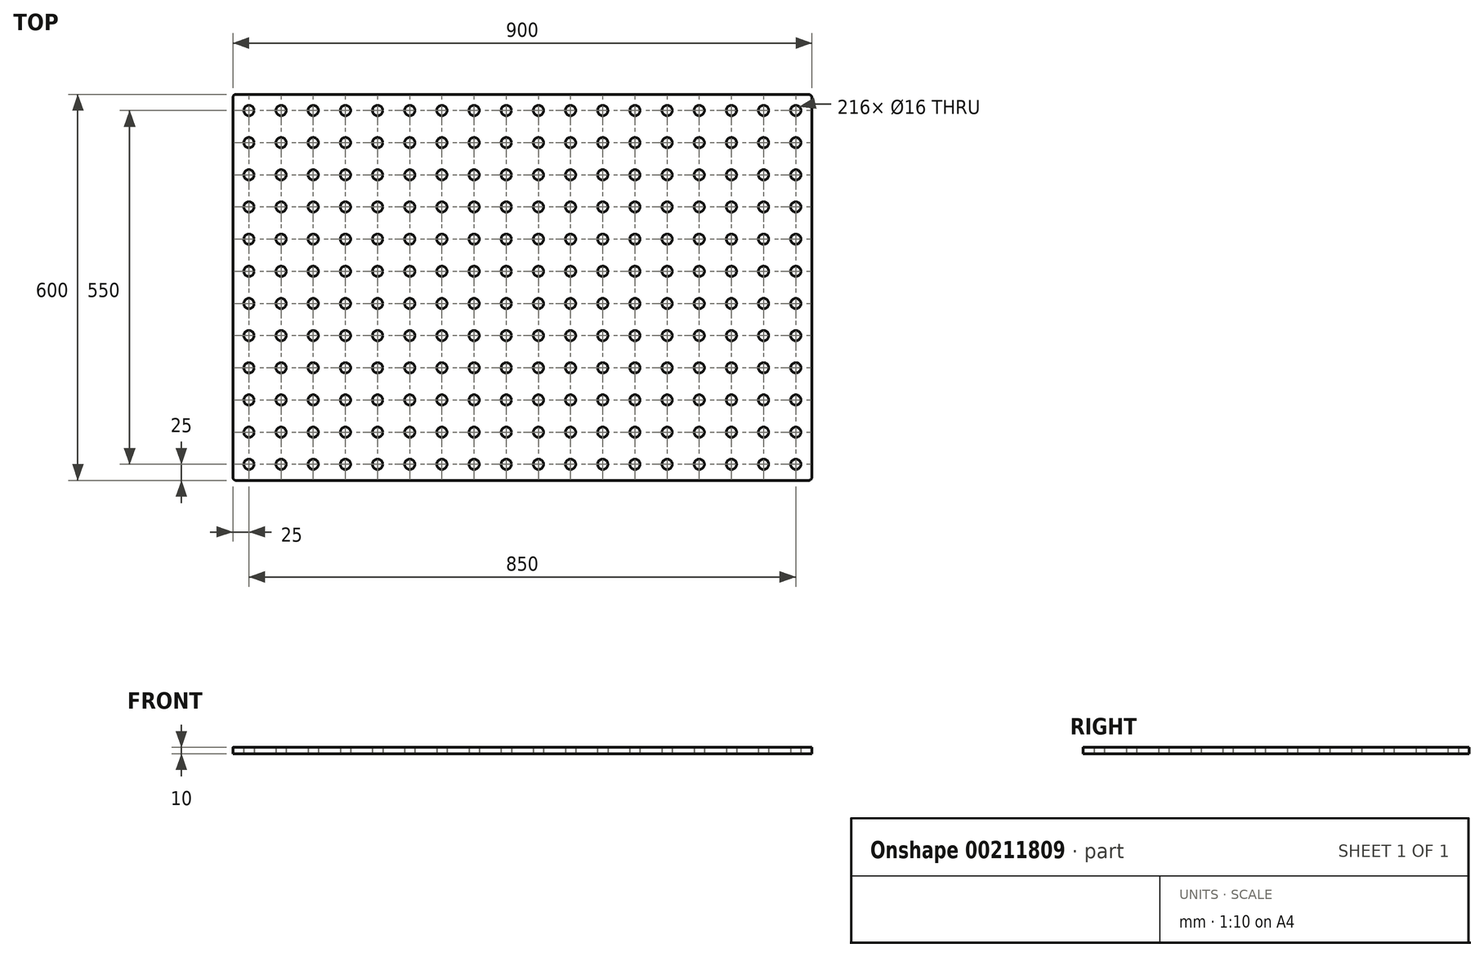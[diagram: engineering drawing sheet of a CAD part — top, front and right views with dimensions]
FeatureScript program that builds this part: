
annotation { "Feature Type Name" : "Feature", "Feature Type Description" : "" }
export const myFeature = defineFeature(function(context is Context, id is Id, definition is map)
    precondition{}
    {
        {
            var Q0;
            Q0=qCreatedBy(makeId("Top.planeOp"),FACE);
            var sketch = newSketch(context, id + "F0", { "sketchPlane" : qUnion([Q0])});
            skLineSegment(sketch, "E0.bottom", {"start": v(5, 0) * mm, "end": v(895, 0) * mm});
            skLineSegment(sketch, "E0.top", {"start": v(5, 600) * mm, "end": v(895, 600) * mm});
            skLineSegment(sketch, "E0.left", {"start": v(0, 5) * mm, "end": v(0, 595) * mm});
            skLineSegment(sketch, "E0.right", {"start": v(900, 5) * mm, "end": v(900, 595) * mm});
            skCircle(sketch, "E1", {"center": v(25, 575) * mm, "radius": 8 * mm});
            skCircle(sketch, "E2.0.1.0", {"center": v(25, 525) * mm, "radius": 8 * mm});
            skCircle(sketch, "E2.0.2.0", {"center": v(25, 475) * mm, "radius": 8 * mm});
            skCircle(sketch, "E2.0.3.0", {"center": v(25, 425) * mm, "radius": 8 * mm});
            skCircle(sketch, "E2.0.4.0", {"center": v(25, 375) * mm, "radius": 8 * mm});
            skCircle(sketch, "E2.0.5.0", {"center": v(25, 325) * mm, "radius": 8 * mm});
            skCircle(sketch, "E2.0.6.0", {"center": v(25, 275) * mm, "radius": 8 * mm});
            skCircle(sketch, "E2.0.7.0", {"center": v(25, 225) * mm, "radius": 8 * mm});
            skCircle(sketch, "E2.0.8.0", {"center": v(25, 175) * mm, "radius": 8 * mm});
            skCircle(sketch, "E2.0.9.0", {"center": v(25, 125) * mm, "radius": 8 * mm});
            skCircle(sketch, "E2.0.10.0", {"center": v(25, 75) * mm, "radius": 8 * mm});
            skCircle(sketch, "E2.0.11.0", {"center": v(25, 25) * mm, "radius": 8 * mm});
            skCircle(sketch, "E2.1.0.0", {"center": v(75, 575) * mm, "radius": 8 * mm});
            skCircle(sketch, "E2.1.1.0", {"center": v(75, 525) * mm, "radius": 8 * mm});
            skCircle(sketch, "E2.1.2.0", {"center": v(75, 475) * mm, "radius": 8 * mm});
            skCircle(sketch, "E2.1.3.0", {"center": v(75, 425) * mm, "radius": 8 * mm});
            skCircle(sketch, "E2.1.4.0", {"center": v(75, 375) * mm, "radius": 8 * mm});
            skCircle(sketch, "E2.1.5.0", {"center": v(75, 325) * mm, "radius": 8 * mm});
            skCircle(sketch, "E2.1.6.0", {"center": v(75, 275) * mm, "radius": 8 * mm});
            skCircle(sketch, "E2.1.7.0", {"center": v(75, 225) * mm, "radius": 8 * mm});
            skCircle(sketch, "E2.1.8.0", {"center": v(75, 175) * mm, "radius": 8 * mm});
            skCircle(sketch, "E2.1.9.0", {"center": v(75, 125) * mm, "radius": 8 * mm});
            skCircle(sketch, "E2.1.10.0", {"center": v(75, 75) * mm, "radius": 8 * mm});
            skCircle(sketch, "E2.1.11.0", {"center": v(75, 25) * mm, "radius": 8 * mm});
            skCircle(sketch, "E2.2.0.0", {"center": v(125, 575) * mm, "radius": 8 * mm});
            skCircle(sketch, "E2.2.1.0", {"center": v(125, 525) * mm, "radius": 8 * mm});
            skCircle(sketch, "E2.2.2.0", {"center": v(125, 475) * mm, "radius": 8 * mm});
            skCircle(sketch, "E2.2.3.0", {"center": v(125, 425) * mm, "radius": 8 * mm});
            skCircle(sketch, "E2.2.4.0", {"center": v(125, 375) * mm, "radius": 8 * mm});
            skCircle(sketch, "E2.2.5.0", {"center": v(125, 325) * mm, "radius": 8 * mm});
            skCircle(sketch, "E2.2.6.0", {"center": v(125, 275) * mm, "radius": 8 * mm});
            skCircle(sketch, "E2.2.7.0", {"center": v(125, 225) * mm, "radius": 8 * mm});
            skCircle(sketch, "E2.2.8.0", {"center": v(125, 175) * mm, "radius": 8 * mm});
            skCircle(sketch, "E2.2.9.0", {"center": v(125, 125) * mm, "radius": 8 * mm});
            skCircle(sketch, "E2.2.10.0", {"center": v(125, 75) * mm, "radius": 8 * mm});
            skCircle(sketch, "E2.2.11.0", {"center": v(125, 25) * mm, "radius": 8 * mm});
            skCircle(sketch, "E2.3.0.0", {"center": v(175, 575) * mm, "radius": 8 * mm});
            skCircle(sketch, "E2.3.1.0", {"center": v(175, 525) * mm, "radius": 8 * mm});
            skCircle(sketch, "E2.3.2.0", {"center": v(175, 475) * mm, "radius": 8 * mm});
            skCircle(sketch, "E2.3.3.0", {"center": v(175, 425) * mm, "radius": 8 * mm});
            skCircle(sketch, "E2.3.4.0", {"center": v(175, 375) * mm, "radius": 8 * mm});
            skCircle(sketch, "E2.3.5.0", {"center": v(175, 325) * mm, "radius": 8 * mm});
            skCircle(sketch, "E2.3.6.0", {"center": v(175, 275) * mm, "radius": 8 * mm});
            skCircle(sketch, "E2.3.7.0", {"center": v(175, 225) * mm, "radius": 8 * mm});
            skCircle(sketch, "E2.3.8.0", {"center": v(175, 175) * mm, "radius": 8 * mm});
            skCircle(sketch, "E2.3.9.0", {"center": v(175, 125) * mm, "radius": 8 * mm});
            skCircle(sketch, "E2.3.10.0", {"center": v(175, 75) * mm, "radius": 8 * mm});
            skCircle(sketch, "E2.3.11.0", {"center": v(175, 25) * mm, "radius": 8 * mm});
            skCircle(sketch, "E2.4.0.0", {"center": v(225, 575) * mm, "radius": 8 * mm});
            skCircle(sketch, "E2.4.1.0", {"center": v(225, 525) * mm, "radius": 8 * mm});
            skCircle(sketch, "E2.4.2.0", {"center": v(225, 475) * mm, "radius": 8 * mm});
            skCircle(sketch, "E2.4.3.0", {"center": v(225, 425) * mm, "radius": 8 * mm});
            skCircle(sketch, "E2.4.4.0", {"center": v(225, 375) * mm, "radius": 8 * mm});
            skCircle(sketch, "E2.4.5.0", {"center": v(225, 325) * mm, "radius": 8 * mm});
            skCircle(sketch, "E2.4.6.0", {"center": v(225, 275) * mm, "radius": 8 * mm});
            skCircle(sketch, "E2.4.7.0", {"center": v(225, 225) * mm, "radius": 8 * mm});
            skCircle(sketch, "E2.4.8.0", {"center": v(225, 175) * mm, "radius": 8 * mm});
            skCircle(sketch, "E2.4.9.0", {"center": v(225, 125) * mm, "radius": 8 * mm});
            skCircle(sketch, "E2.4.10.0", {"center": v(225, 75) * mm, "radius": 8 * mm});
            skCircle(sketch, "E2.4.11.0", {"center": v(225, 25) * mm, "radius": 8 * mm});
            skCircle(sketch, "E2.5.0.0", {"center": v(275, 575) * mm, "radius": 8 * mm});
            skCircle(sketch, "E2.5.1.0", {"center": v(275, 525) * mm, "radius": 8 * mm});
            skCircle(sketch, "E2.5.2.0", {"center": v(275, 475) * mm, "radius": 8 * mm});
            skCircle(sketch, "E2.5.3.0", {"center": v(275, 425) * mm, "radius": 8 * mm});
            skCircle(sketch, "E2.5.4.0", {"center": v(275, 375) * mm, "radius": 8 * mm});
            skCircle(sketch, "E2.5.5.0", {"center": v(275, 325) * mm, "radius": 8 * mm});
            skCircle(sketch, "E2.5.6.0", {"center": v(275, 275) * mm, "radius": 8 * mm});
            skCircle(sketch, "E2.5.7.0", {"center": v(275, 225) * mm, "radius": 8 * mm});
            skCircle(sketch, "E2.5.8.0", {"center": v(275, 175) * mm, "radius": 8 * mm});
            skCircle(sketch, "E2.5.9.0", {"center": v(275, 125) * mm, "radius": 8 * mm});
            skCircle(sketch, "E2.5.10.0", {"center": v(275, 75) * mm, "radius": 8 * mm});
            skCircle(sketch, "E2.5.11.0", {"center": v(275, 25) * mm, "radius": 8 * mm});
            skCircle(sketch, "E2.6.0.0", {"center": v(325, 575) * mm, "radius": 8 * mm});
            skCircle(sketch, "E2.6.1.0", {"center": v(325, 525) * mm, "radius": 8 * mm});
            skCircle(sketch, "E2.6.2.0", {"center": v(325, 475) * mm, "radius": 8 * mm});
            skCircle(sketch, "E2.6.3.0", {"center": v(325, 425) * mm, "radius": 8 * mm});
            skCircle(sketch, "E2.6.4.0", {"center": v(325, 375) * mm, "radius": 8 * mm});
            skCircle(sketch, "E2.6.5.0", {"center": v(325, 325) * mm, "radius": 8 * mm});
            skCircle(sketch, "E2.6.6.0", {"center": v(325, 275) * mm, "radius": 8 * mm});
            skCircle(sketch, "E2.6.7.0", {"center": v(325, 225) * mm, "radius": 8 * mm});
            skCircle(sketch, "E2.6.8.0", {"center": v(325, 175) * mm, "radius": 8 * mm});
            skCircle(sketch, "E2.6.9.0", {"center": v(325, 125) * mm, "radius": 8 * mm});
            skCircle(sketch, "E2.6.10.0", {"center": v(325, 75) * mm, "radius": 8 * mm});
            skCircle(sketch, "E2.6.11.0", {"center": v(325, 25) * mm, "radius": 8 * mm});
            skCircle(sketch, "E2.7.0.0", {"center": v(375, 575) * mm, "radius": 8 * mm});
            skCircle(sketch, "E2.7.1.0", {"center": v(375, 525) * mm, "radius": 8 * mm});
            skCircle(sketch, "E2.7.2.0", {"center": v(375, 475) * mm, "radius": 8 * mm});
            skCircle(sketch, "E2.7.3.0", {"center": v(375, 425) * mm, "radius": 8 * mm});
            skCircle(sketch, "E2.7.4.0", {"center": v(375, 375) * mm, "radius": 8 * mm});
            skCircle(sketch, "E2.7.5.0", {"center": v(375, 325) * mm, "radius": 8 * mm});
            skCircle(sketch, "E2.7.6.0", {"center": v(375, 275) * mm, "radius": 8 * mm});
            skCircle(sketch, "E2.7.7.0", {"center": v(375, 225) * mm, "radius": 8 * mm});
            skCircle(sketch, "E2.7.8.0", {"center": v(375, 175) * mm, "radius": 8 * mm});
            skCircle(sketch, "E2.7.9.0", {"center": v(375, 125) * mm, "radius": 8 * mm});
            skCircle(sketch, "E2.7.10.0", {"center": v(375, 75) * mm, "radius": 8 * mm});
            skCircle(sketch, "E2.7.11.0", {"center": v(375, 25) * mm, "radius": 8 * mm});
            skCircle(sketch, "E2.8.0.0", {"center": v(425, 575) * mm, "radius": 8 * mm});
            skCircle(sketch, "E2.8.1.0", {"center": v(425, 525) * mm, "radius": 8 * mm});
            skCircle(sketch, "E2.8.2.0", {"center": v(425, 475) * mm, "radius": 8 * mm});
            skCircle(sketch, "E2.8.3.0", {"center": v(425, 425) * mm, "radius": 8 * mm});
            skCircle(sketch, "E2.8.4.0", {"center": v(425, 375) * mm, "radius": 8 * mm});
            skCircle(sketch, "E2.8.5.0", {"center": v(425, 325) * mm, "radius": 8 * mm});
            skCircle(sketch, "E2.8.6.0", {"center": v(425, 275) * mm, "radius": 8 * mm});
            skCircle(sketch, "E2.8.7.0", {"center": v(425, 225) * mm, "radius": 8 * mm});
            skCircle(sketch, "E2.8.8.0", {"center": v(425, 175) * mm, "radius": 8 * mm});
            skCircle(sketch, "E2.8.9.0", {"center": v(425, 125) * mm, "radius": 8 * mm});
            skCircle(sketch, "E2.8.10.0", {"center": v(425, 75) * mm, "radius": 8 * mm});
            skCircle(sketch, "E2.8.11.0", {"center": v(425, 25) * mm, "radius": 8 * mm});
            skCircle(sketch, "E2.9.0.0", {"center": v(475, 575) * mm, "radius": 8 * mm});
            skCircle(sketch, "E2.9.1.0", {"center": v(475, 525) * mm, "radius": 8 * mm});
            skCircle(sketch, "E2.9.2.0", {"center": v(475, 475) * mm, "radius": 8 * mm});
            skCircle(sketch, "E2.9.3.0", {"center": v(475, 425) * mm, "radius": 8 * mm});
            skCircle(sketch, "E2.9.4.0", {"center": v(475, 375) * mm, "radius": 8 * mm});
            skCircle(sketch, "E2.9.5.0", {"center": v(475, 325) * mm, "radius": 8 * mm});
            skCircle(sketch, "E2.9.6.0", {"center": v(475, 275) * mm, "radius": 8 * mm});
            skCircle(sketch, "E2.9.7.0", {"center": v(475, 225) * mm, "radius": 8 * mm});
            skCircle(sketch, "E2.9.8.0", {"center": v(475, 175) * mm, "radius": 8 * mm});
            skCircle(sketch, "E2.9.9.0", {"center": v(475, 125) * mm, "radius": 8 * mm});
            skCircle(sketch, "E2.9.10.0", {"center": v(475, 75) * mm, "radius": 8 * mm});
            skCircle(sketch, "E2.9.11.0", {"center": v(475, 25) * mm, "radius": 8 * mm});
            skCircle(sketch, "E2.10.0.0", {"center": v(525, 575) * mm, "radius": 8 * mm});
            skCircle(sketch, "E2.10.1.0", {"center": v(525, 525) * mm, "radius": 8 * mm});
            skCircle(sketch, "E2.10.2.0", {"center": v(525, 475) * mm, "radius": 8 * mm});
            skCircle(sketch, "E2.10.3.0", {"center": v(525, 425) * mm, "radius": 8 * mm});
            skCircle(sketch, "E2.10.4.0", {"center": v(525, 375) * mm, "radius": 8 * mm});
            skCircle(sketch, "E2.10.5.0", {"center": v(525, 325) * mm, "radius": 8 * mm});
            skCircle(sketch, "E2.10.6.0", {"center": v(525, 275) * mm, "radius": 8 * mm});
            skCircle(sketch, "E2.10.7.0", {"center": v(525, 225) * mm, "radius": 8 * mm});
            skCircle(sketch, "E2.10.8.0", {"center": v(525, 175) * mm, "radius": 8 * mm});
            skCircle(sketch, "E2.10.9.0", {"center": v(525, 125) * mm, "radius": 8 * mm});
            skCircle(sketch, "E2.10.10.0", {"center": v(525, 75) * mm, "radius": 8 * mm});
            skCircle(sketch, "E2.10.11.0", {"center": v(525, 25) * mm, "radius": 8 * mm});
            skCircle(sketch, "E2.11.0.0", {"center": v(575, 575) * mm, "radius": 8 * mm});
            skCircle(sketch, "E2.11.1.0", {"center": v(575, 525) * mm, "radius": 8 * mm});
            skCircle(sketch, "E2.11.2.0", {"center": v(575, 475) * mm, "radius": 8 * mm});
            skCircle(sketch, "E2.11.3.0", {"center": v(575, 425) * mm, "radius": 8 * mm});
            skCircle(sketch, "E2.11.4.0", {"center": v(575, 375) * mm, "radius": 8 * mm});
            skCircle(sketch, "E2.11.5.0", {"center": v(575, 325) * mm, "radius": 8 * mm});
            skCircle(sketch, "E2.11.6.0", {"center": v(575, 275) * mm, "radius": 8 * mm});
            skCircle(sketch, "E2.11.7.0", {"center": v(575, 225) * mm, "radius": 8 * mm});
            skCircle(sketch, "E2.11.8.0", {"center": v(575, 175) * mm, "radius": 8 * mm});
            skCircle(sketch, "E2.11.9.0", {"center": v(575, 125) * mm, "radius": 8 * mm});
            skCircle(sketch, "E2.11.10.0", {"center": v(575, 75) * mm, "radius": 8 * mm});
            skCircle(sketch, "E2.11.11.0", {"center": v(575, 25) * mm, "radius": 8 * mm});
            skCircle(sketch, "E2.12.0.0", {"center": v(625, 575) * mm, "radius": 8 * mm});
            skCircle(sketch, "E2.12.1.0", {"center": v(625, 525) * mm, "radius": 8 * mm});
            skCircle(sketch, "E2.12.2.0", {"center": v(625, 475) * mm, "radius": 8 * mm});
            skCircle(sketch, "E2.12.3.0", {"center": v(625, 425) * mm, "radius": 8 * mm});
            skCircle(sketch, "E2.12.4.0", {"center": v(625, 375) * mm, "radius": 8 * mm});
            skCircle(sketch, "E2.12.5.0", {"center": v(625, 325) * mm, "radius": 8 * mm});
            skCircle(sketch, "E2.12.6.0", {"center": v(625, 275) * mm, "radius": 8 * mm});
            skCircle(sketch, "E2.12.7.0", {"center": v(625, 225) * mm, "radius": 8 * mm});
            skCircle(sketch, "E2.12.8.0", {"center": v(625, 175) * mm, "radius": 8 * mm});
            skCircle(sketch, "E2.12.9.0", {"center": v(625, 125) * mm, "radius": 8 * mm});
            skCircle(sketch, "E2.12.10.0", {"center": v(625, 75) * mm, "radius": 8 * mm});
            skCircle(sketch, "E2.12.11.0", {"center": v(625, 25) * mm, "radius": 8 * mm});
            skCircle(sketch, "E2.13.0.0", {"center": v(675, 575) * mm, "radius": 8 * mm});
            skCircle(sketch, "E2.13.1.0", {"center": v(675, 525) * mm, "radius": 8 * mm});
            skCircle(sketch, "E2.13.2.0", {"center": v(675, 475) * mm, "radius": 8 * mm});
            skCircle(sketch, "E2.13.3.0", {"center": v(675, 425) * mm, "radius": 8 * mm});
            skCircle(sketch, "E2.13.4.0", {"center": v(675, 375) * mm, "radius": 8 * mm});
            skCircle(sketch, "E2.13.5.0", {"center": v(675, 325) * mm, "radius": 8 * mm});
            skCircle(sketch, "E2.13.6.0", {"center": v(675, 275) * mm, "radius": 8 * mm});
            skCircle(sketch, "E2.13.7.0", {"center": v(675, 225) * mm, "radius": 8 * mm});
            skCircle(sketch, "E2.13.8.0", {"center": v(675, 175) * mm, "radius": 8 * mm});
            skCircle(sketch, "E2.13.9.0", {"center": v(675, 125) * mm, "radius": 8 * mm});
            skCircle(sketch, "E2.13.10.0", {"center": v(675, 75) * mm, "radius": 8 * mm});
            skCircle(sketch, "E2.13.11.0", {"center": v(675, 25) * mm, "radius": 8 * mm});
            skCircle(sketch, "E2.14.0.0", {"center": v(725, 575) * mm, "radius": 8 * mm});
            skCircle(sketch, "E2.14.1.0", {"center": v(725, 525) * mm, "radius": 8 * mm});
            skCircle(sketch, "E2.14.2.0", {"center": v(725, 475) * mm, "radius": 8 * mm});
            skCircle(sketch, "E2.14.3.0", {"center": v(725, 425) * mm, "radius": 8 * mm});
            skCircle(sketch, "E2.14.4.0", {"center": v(725, 375) * mm, "radius": 8 * mm});
            skCircle(sketch, "E2.14.5.0", {"center": v(725, 325) * mm, "radius": 8 * mm});
            skCircle(sketch, "E2.14.6.0", {"center": v(725, 275) * mm, "radius": 8 * mm});
            skCircle(sketch, "E2.14.7.0", {"center": v(725, 225) * mm, "radius": 8 * mm});
            skCircle(sketch, "E2.14.8.0", {"center": v(725, 175) * mm, "radius": 8 * mm});
            skCircle(sketch, "E2.14.9.0", {"center": v(725, 125) * mm, "radius": 8 * mm});
            skCircle(sketch, "E2.14.10.0", {"center": v(725, 75) * mm, "radius": 8 * mm});
            skCircle(sketch, "E2.14.11.0", {"center": v(725, 25) * mm, "radius": 8 * mm});
            skCircle(sketch, "E2.15.0.0", {"center": v(775, 575) * mm, "radius": 8 * mm});
            skCircle(sketch, "E2.15.1.0", {"center": v(775, 525) * mm, "radius": 8 * mm});
            skCircle(sketch, "E2.15.2.0", {"center": v(775, 475) * mm, "radius": 8 * mm});
            skCircle(sketch, "E2.15.3.0", {"center": v(775, 425) * mm, "radius": 8 * mm});
            skCircle(sketch, "E2.15.4.0", {"center": v(775, 375) * mm, "radius": 8 * mm});
            skCircle(sketch, "E2.15.5.0", {"center": v(775, 325) * mm, "radius": 8 * mm});
            skCircle(sketch, "E2.15.6.0", {"center": v(775, 275) * mm, "radius": 8 * mm});
            skCircle(sketch, "E2.15.7.0", {"center": v(775, 225) * mm, "radius": 8 * mm});
            skCircle(sketch, "E2.15.8.0", {"center": v(775, 175) * mm, "radius": 8 * mm});
            skCircle(sketch, "E2.15.9.0", {"center": v(775, 125) * mm, "radius": 8 * mm});
            skCircle(sketch, "E2.15.10.0", {"center": v(775, 75) * mm, "radius": 8 * mm});
            skCircle(sketch, "E2.15.11.0", {"center": v(775, 25) * mm, "radius": 8 * mm});
            skCircle(sketch, "E2.16.0.0", {"center": v(825, 575) * mm, "radius": 8 * mm});
            skCircle(sketch, "E2.16.1.0", {"center": v(825, 525) * mm, "radius": 8 * mm});
            skCircle(sketch, "E2.16.2.0", {"center": v(825, 475) * mm, "radius": 8 * mm});
            skCircle(sketch, "E2.16.3.0", {"center": v(825, 425) * mm, "radius": 8 * mm});
            skCircle(sketch, "E2.16.4.0", {"center": v(825, 375) * mm, "radius": 8 * mm});
            skCircle(sketch, "E2.16.5.0", {"center": v(825, 325) * mm, "radius": 8 * mm});
            skCircle(sketch, "E2.16.6.0", {"center": v(825, 275) * mm, "radius": 8 * mm});
            skCircle(sketch, "E2.16.7.0", {"center": v(825, 225) * mm, "radius": 8 * mm});
            skCircle(sketch, "E2.16.8.0", {"center": v(825, 175) * mm, "radius": 8 * mm});
            skCircle(sketch, "E2.16.9.0", {"center": v(825, 125) * mm, "radius": 8 * mm});
            skCircle(sketch, "E2.16.10.0", {"center": v(825, 75) * mm, "radius": 8 * mm});
            skCircle(sketch, "E2.16.11.0", {"center": v(825, 25) * mm, "radius": 8 * mm});
            skCircle(sketch, "E2.17.0.0", {"center": v(875, 575) * mm, "radius": 8 * mm});
            skCircle(sketch, "E2.17.1.0", {"center": v(875, 525) * mm, "radius": 8 * mm});
            skCircle(sketch, "E2.17.2.0", {"center": v(875, 475) * mm, "radius": 8 * mm});
            skCircle(sketch, "E2.17.3.0", {"center": v(875, 425) * mm, "radius": 8 * mm});
            skCircle(sketch, "E2.17.4.0", {"center": v(875, 375) * mm, "radius": 8 * mm});
            skCircle(sketch, "E2.17.5.0", {"center": v(875, 325) * mm, "radius": 8 * mm});
            skCircle(sketch, "E2.17.6.0", {"center": v(875, 275) * mm, "radius": 8 * mm});
            skCircle(sketch, "E2.17.7.0", {"center": v(875, 225) * mm, "radius": 8 * mm});
            skCircle(sketch, "E2.17.8.0", {"center": v(875, 175) * mm, "radius": 8 * mm});
            skCircle(sketch, "E2.17.9.0", {"center": v(875, 125) * mm, "radius": 8 * mm});
            skCircle(sketch, "E2.17.10.0", {"center": v(875, 75) * mm, "radius": 8 * mm});
            skCircle(sketch, "E2.17.11.0", {"center": v(875, 25) * mm, "radius": 8 * mm});
            skLineSegment(sketch, "E2.direction1", {"start": v(25, 575) * mm, "end": v(75, 575) * mm, "construction": true});
            skLineSegment(sketch, "E2.direction2", {"start": v(25, 575) * mm, "end": v(25, 525) * mm, "construction": true});
            skPoint(sketch, "E3.visualSharp", {"position": v(900, 600) * mm});
            skArc(sketch, "E3.filletArc", {"start": v(900, 595) * mm, "mid": v(898.54, 598.54) * mm, "end": v(895, 600) * mm});
            skPoint(sketch, "E4.visualSharp", {"position": v(900, 0) * mm});
            skArc(sketch, "E4.filletArc", {"start": v(895, 0) * mm, "mid": v(898.54, 1.46) * mm, "end": v(900, 5) * mm});
            skPoint(sketch, "E5.visualSharp", {"position": v(0, 0) * mm});
            skArc(sketch, "E5.filletArc", {"start": v(0, 5) * mm, "mid": v(1.46, 1.46) * mm, "end": v(5, 0) * mm});
            skPoint(sketch, "E6.visualSharp", {"position": v(0, 600) * mm});
            skArc(sketch, "E6.filletArc", {"start": v(5, 600) * mm, "mid": v(1.46, 598.54) * mm, "end": v(0, 595) * mm});
            skSolve(sketch);
        }
        {
            var Q0;
            Q0=qSketchRegion(id+"F0",true);
            extrude(context, id + "F1", {"entities" : qUnion([Q0]), "depth" : 10 * mm});
        }
    });
